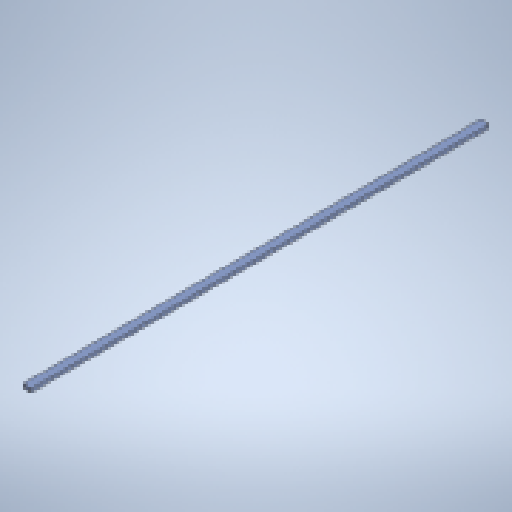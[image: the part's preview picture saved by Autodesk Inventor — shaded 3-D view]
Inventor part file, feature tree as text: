
AUTODESK INVENTOR PART (.ipt)
format: ipt  version: 2025.1 (Build 291241020, 241B)  size: 138,752 bytes
history: native  units: in
note: dims shown in document units (in); Inventor stores cm internally (conversion verified against a paired STEP export)
features: extrude x1, sketch x1, other x1
ambient origin geometry x8: Origin, YZ Plane, XZ Plane, XY Plane, X Axis, Y Axis, Z Axis, Center Point
bodies: Solid1 (feature_tree)
feature tree (3):
  extrude  "Extrusion1"  Depth=1.5in
  sketch  "Sketch1"  dims[d0=3.5in d1=1.5in d2=192.0in d3=0.0in]
  other  "Finish1"
